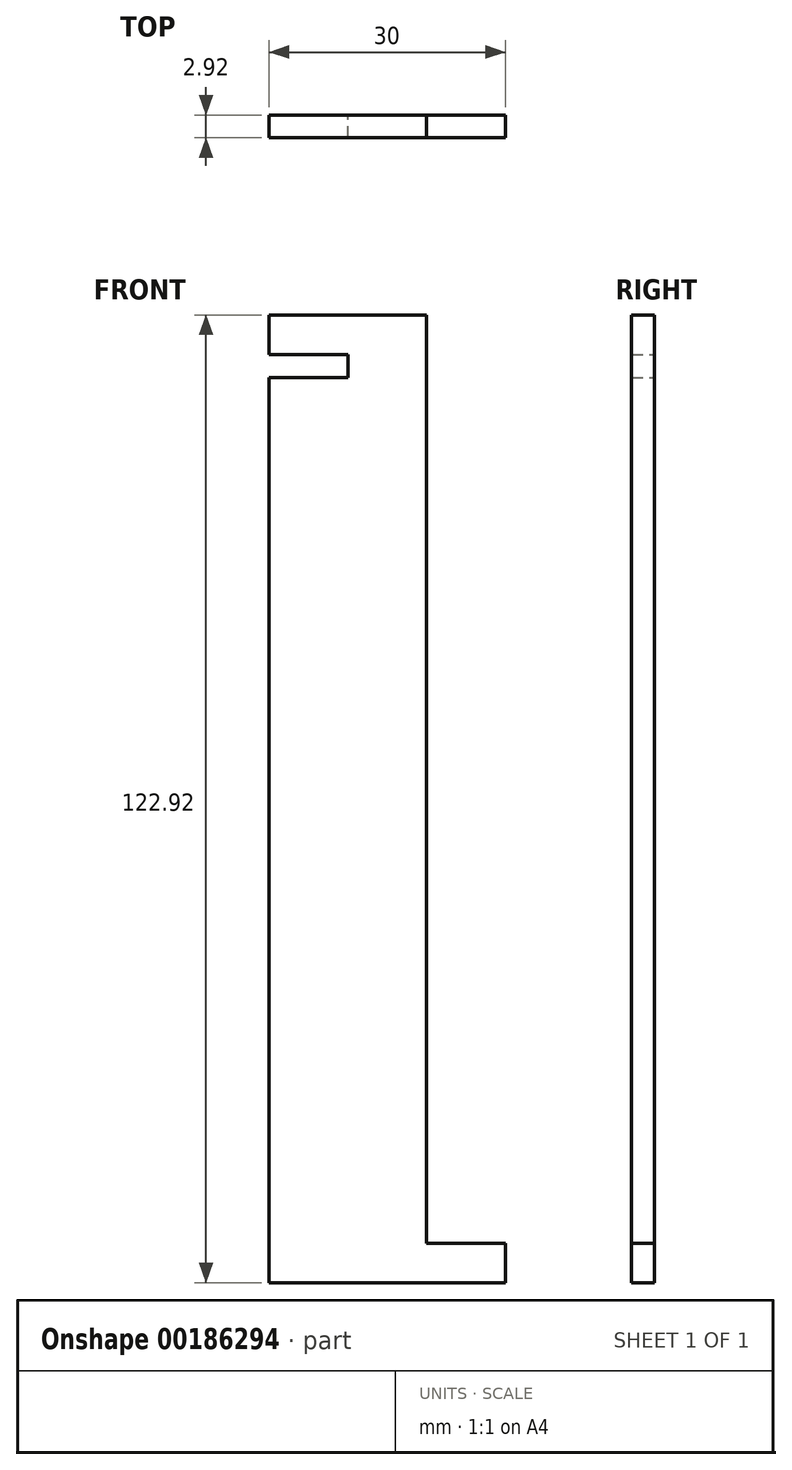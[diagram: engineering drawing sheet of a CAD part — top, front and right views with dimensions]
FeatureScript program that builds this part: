
annotation { "Feature Type Name" : "Feature", "Feature Type Description" : "" }
export const myFeature = defineFeature(function(context is Context, id is Id, definition is map)
    precondition{}
    {
        {
            assignVariable(context, id + "F0", {"name" : "e", "anyValue" : 2.92 * mm});
        }
        {
            var Q0;
            Q0=qCreatedBy(makeId("Front.planeOp"),FACE);
            var sketch = newSketch(context, id + "F1", { "sketchPlane" : qUnion([Q0])});
            skLineSegment(sketch, "E0.bottom", {"start": v(-30, 122.92) * mm, "end": v(-10, 122.92) * mm});
            skLineSegment(sketch, "E0.top", {"start": v(-30, 0) * mm, "end": v(0, 0) * mm});
            skLineSegment(sketch, "E0.left", {"start": v(-30, 122.92) * mm, "end": v(-30, 117.92) * mm});
            skLineSegment(sketch, "E0.right", {"start": v(-10, 122.92) * mm, "end": v(-10, 5) * mm});
            skLineSegment(sketch, "E1.bottom", {"start": v(-30, 117.92) * mm, "end": v(-20, 117.92) * mm});
            skLineSegment(sketch, "E1.top", {"start": v(-30, 115) * mm, "end": v(-20, 115) * mm});
            skLineSegment(sketch, "E1.right", {"start": v(-20, 117.92) * mm, "end": v(-20, 115) * mm});
            skLineSegment(sketch, "E2.top", {"start": v(-10, 5) * mm, "end": v(0, 5) * mm});
            skLineSegment(sketch, "E2.right", {"start": v(0, 5) * mm, "end": v(0, 0) * mm});
            skLineSegment(sketch, "E3.trimOffspring", {"start": v(-30, 115) * mm, "end": v(-30, 0) * mm});
            skSolve(sketch);
        }
        {
            var Q0;
            Q0 = qSketchRegion(id + "F1", true);
            extrude(context, id + "F2", {"entities" : qUnion([Q0]), "depth" : getVariable(context, 'e')});
        }
    });
